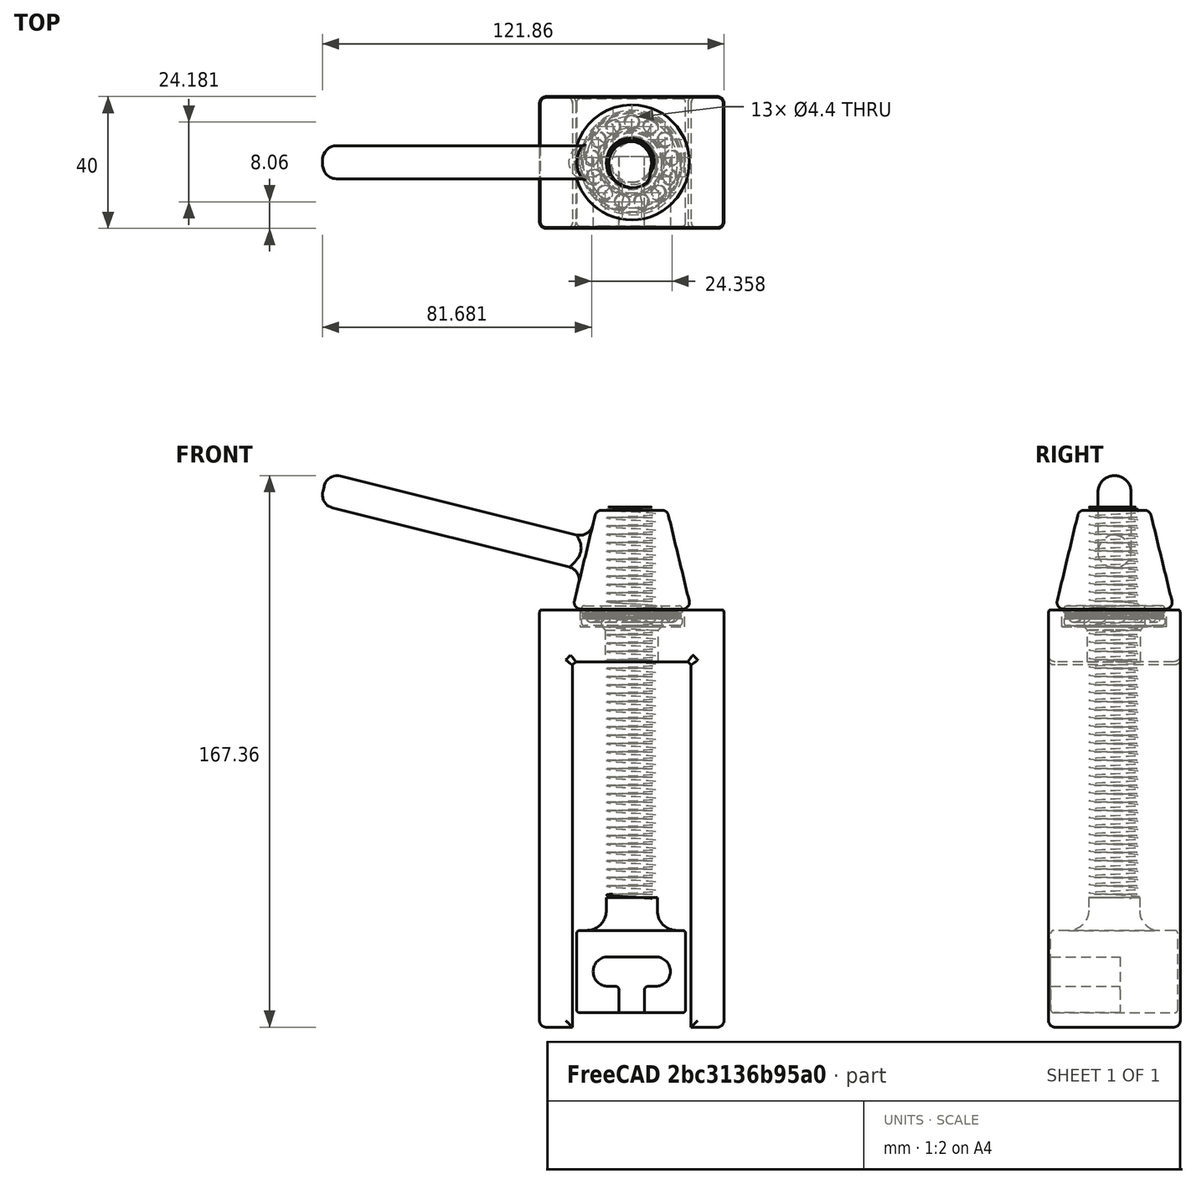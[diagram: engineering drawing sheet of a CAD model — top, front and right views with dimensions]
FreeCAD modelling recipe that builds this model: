
FCSTD DOCUMENT  (FreeCAD 0.21R33771 (Git))
Label: sjemnik
License: All rights reserved
LicenseURL: http://en.wikipedia.org/wiki/All_rights_reserved
objects: Sketcher::SketchObject×25, PartDesign::Fillet×14, PartDesign::Pad×9, PartDesign::Pocket×8, PartDesign::Body×8, PartDesign::Chamfer×3, PartDesign::Plane×3, Part::Part2DObjectPython×2, Part::Helix×2, PartDesign::AdditivePipe×2, PartDesign::Groove×2, PartDesign::CoordinateSystem×1, PartDesign::Line×1, PartDesign::Revolution×1, Part::FeaturePython×1, PartDesign::PolarPattern×1, PartDesign::AdditiveLoft×1, Part::Cut×1
note: 125 computed .brp shape members not serialized (recipe doc carries the construction recipe); baked Part::Feature solids carry a one-line shape summary decoded from their .brp

FEATURE [Sketcher::SketchObject] Sketch
  FullyConstrained = false
  MapMode = 5
  Placement = pos=(0,0,0) rot=(1,0,0;1.5708rad)
  Support = -> [XZ_Plane]
  sketch-geometry (8):
    g0: LineSegment StartX=18 StartY=17.0219 StartZ=0 EndX=-18 EndY=17.0219 EndZ=0
    g1: LineSegment StartX=-18 StartY=17.0219 StartZ=0 EndX=-18 EndY=-93.8501 EndZ=0
    g2: LineSegment StartX=-18 StartY=-93.8501 StartZ=0 EndX=-28 EndY=-93.8501 EndZ=0
    g3: LineSegment StartX=-28 StartY=-93.8501 StartZ=0 EndX=-28 EndY=33.6857 EndZ=0
    g4: LineSegment StartX=28 StartY=33.6857 StartZ=0 EndX=-28 EndY=33.6857 EndZ=0
    g5: LineSegment StartX=18 StartY=17.0219 StartZ=0 EndX=18 EndY=-93.8501 EndZ=0
    g6: LineSegment StartX=18 StartY=-93.8501 StartZ=0 EndX=28 EndY=-93.8501 EndZ=0
    g7: LineSegment StartX=28 StartY=-93.8501 StartZ=0 EndX=28 EndY=33.6857 EndZ=0
  constraints (20):
    c: Horizontal(g0)
    c: Symmetric(g4,g3,g-2)
    c: Coincident(g1,g2)
    c: Coincident(g2,g3)
    c: Horizontal(g2)
    c: Vertical(g1)
    c: Vertical(g3)
    c: Coincident(g5,g6)
    c: Coincident(g6,g7)
    c: Coincident(g7,g4)
    c: Horizontal(g6)
    c: Vertical(g5)
    c: Vertical(g7)
    c: Equal(g2,g6)
    c: Coincident(g5,g0)
    c: Coincident(g0,g1)
    c: Coincident(g4,g3)
    c: Equal(g1,g5)
    c: Distance(g4) = 56
    c: Distance(g0) = 36
FEATURE [PartDesign::Pad] Pad
  Direction = (0,-1,2e-16)
  Length = 40
  Length2 = 10
  Placement = pos=(0,0,0) rot=(1,0,0;1.5708rad)
  Profile = -> Sketch
  ReferenceAxis = -> Sketch [N_Axis]
  Refine = true
  Type = 0
FEATURE [PartDesign::Fillet] Fillet
  Base = -> Pad [Face5,Face10,Face6,Face4,Face9]
  BaseFeature = -> Pad
  Placement = pos=(0,0,0) rot=(1,0,0;1.5708rad)
  Radius = 2
  Refine = true
  SupportTransform = false
  UseAllEdges = false
FEATURE [PartDesign::Chamfer] Chamfer
  Angle = 45
  Base = -> Fillet [Edge1,Edge4]
  BaseFeature = -> Fillet
  ChamferType = 0
  FlipDirection = false
  Placement = pos=(0,0,0) rot=(1,0,0;1.5708rad)
  Refine = true
  Size = 1
  Size2 = 1
  SupportTransform = false
  UseAllEdges = false
FEATURE [Sketcher::SketchObject] Sketch001
  FullyConstrained = false
  MapMode = 5
  Placement = pos=(0,2.23e-14,33.6857) rot=(0,0,1;3.14159rad)
  Support = -> [Chamfer]
  sketch-geometry (2):
    g0: Circle CenterX=-0.164408 CenterY=20.0241 CenterZ=0 NormalX=0 NormalY=0 NormalZ=1 AngleXU=0 Radius=20.0248
    g1: Circle CenterX=-0.164408 CenterY=20.0241 CenterZ=0 NormalX=0 NormalY=0 NormalZ=1 AngleXU=0 Radius=15.8641
  constraints (2):
    c: PointOnObject(g-1,g0)
    c: Coincident(g1,g0)
FEATURE [PartDesign::Pocket] Pocket
  BaseFeature = -> Chamfer
  Direction = (0,0,-1)
  Length = 6
  Length2 = 5
  Placement = pos=(0,0,0) rot=(1,0,0;1.5708rad)
  Profile = -> Sketch001
  ReferenceAxis = -> Sketch001 [N_Axis]
  Refine = true
  Type = 0
FEATURE [PartDesign::Fillet] Fillet001
  Base = -> Pocket [Edge85]
  BaseFeature = -> Pocket
  Placement = pos=(0,0,0) rot=(1,0,0;1.5708rad)
  Radius = 1
  Refine = true
  SupportTransform = false
  UseAllEdges = false
FEATURE [Sketcher::SketchObject] Sketch002
  FullyConstrained = false
  MapMode = 5
  Placement = pos=(0,6.1e-15,27.6857) rot=(0,0,1;3.14159rad)
  Support = -> [Fillet001]
  sketch-geometry (1):
    g0: Circle CenterX=0 CenterY=20.1421 CenterZ=0 NormalX=0 NormalY=0 NormalZ=1 AngleXU=0 Radius=8.03905
  constraints (1):
    c: PointOnObject(g0,g-2)
FEATURE [PartDesign::Pocket] Pocket001
  BaseFeature = -> Fillet001
  Direction = (0,2e-16,-1)
  Length = 15
  Length2 = 5
  Placement = pos=(0,0,0) rot=(1,0,0;1.5708rad)
  Profile = -> Sketch002
  ReferenceAxis = -> Sketch002 [N_Axis]
  Refine = true
  Type = 0
FEATURE [PartDesign::Chamfer] Chamfer001
  Angle = 45
  Base = -> Pocket001 [Edge54]
  BaseFeature = -> Pocket001
  ChamferType = 0
  FlipDirection = false
  Placement = pos=(0,0,0) rot=(1,0,0;1.5708rad)
  Refine = true
  Size = 1
  Size2 = 1
  SupportTransform = false
  UseAllEdges = false
FEATURE [Sketcher::SketchObject] Sketch003
  FullyConstrained = false
  MapMode = 5
  Support = -> [XY_Plane001]
  sketch-geometry (4):
    g0: LineSegment StartX=16.3519 StartY=-0.720672 StartZ=0 EndX=-16.7624 EndY=-0.720672 EndZ=0
    g1: LineSegment StartX=-16.7624 StartY=-0.720672 StartZ=0 EndX=-16.7624 EndY=-39.3105 EndZ=0
    g2: LineSegment StartX=-16.7624 StartY=-39.3105 StartZ=0 EndX=16.3519 EndY=-39.3105 EndZ=0
    g3: LineSegment StartX=16.3519 StartY=-39.3105 StartZ=0 EndX=16.3519 EndY=-0.720672 EndZ=0
  constraints (8):
    c: Coincident(g0,g1)
    c: Coincident(g1,g2)
    c: Coincident(g2,g3)
    c: Coincident(g3,g0)
    c: Horizontal(g0)
    c: Horizontal(g2)
    c: Vertical(g1)
    c: Vertical(g3)
FEATURE [PartDesign::Pad] Pad001
  Direction = (0,0,1)
  Length = 25
  Length2 = 10
  Midplane = true
  Profile = -> Sketch003
  ReferenceAxis = -> Sketch003 [N_Axis]
  Refine = true
  Type = 0
FEATURE [PartDesign::Fillet] Fillet002
  Base = -> Pad001 [Face6,Face3,Face5,Face1,Face2]
  BaseFeature = -> Pad001
  Radius = 1
  Refine = true
  SupportTransform = false
  UseAllEdges = false
FEATURE [Sketcher::SketchObject] Sketch004
  FullyConstrained = false
  MapMode = 5
  Placement = pos=(0,-39.3105,0) rot=(1,0,0;1.5708rad)
  Support = -> [Fillet002]
  sketch-geometry (8):
    g0: ArcOfCircle CenterX=0 CenterY=-15.596 CenterZ=0 NormalX=0 NormalY=0 NormalZ=1 AngleXU=0 Radius=3.88762 StartAngle=3.14159 EndAngle=6.28319
    g1: LineSegment StartX=-3.88762 StartY=-4.48111 StartZ=0 EndX=-3.88762 EndY=-15.596 EndZ=0
    g2: LineSegment StartX=3.88762 StartY=-15.596 StartZ=0 EndX=3.88762 EndY=-4.48111 EndZ=0
    g3: ArcOfCircle CenterX=-7.23544 CenterY=0 CenterZ=0 NormalX=0 NormalY=0 NormalZ=1 AngleXU=0 Radius=4.48111 StartAngle=1.5708 EndAngle=4.71239
    g4: ArcOfCircle CenterX=7.23544 CenterY=0 CenterZ=0 NormalX=0 NormalY=0 NormalZ=1 AngleXU=0 Radius=4.48111 StartAngle=4.71239 EndAngle=7.85398
    g5: LineSegment StartX=-7.23544 StartY=-4.48111 StartZ=0 EndX=-3.88762 EndY=-4.48111 EndZ=0
    g6: LineSegment StartX=7.23544 StartY=4.48111 StartZ=0 EndX=-7.23544 EndY=4.48111 EndZ=0
    g7: LineSegment StartX=3.88762 StartY=-4.48111 StartZ=0 EndX=7.23544 EndY=-4.48111 EndZ=0
  constraints (11):
    c: Tangent(g1,g0) = -1.5708
    c: Tangent(g0,g2) = -1.5708
    c: PointOnObject(g0,g-2)
    c: Tangent(g3,g5) = -1.5708
    c: Coincident(g7,g4) = -1.5708
    c: Tangent(g4,g6) = -1.5708
    c: Tangent(g6,g3) = -1.5708
    c: Equal(g3,g4)
    c: PointOnObject(g3,g-1)
    c: Coincident(g5,g1)
    c: Coincident(g7,g2)
FEATURE [PartDesign::Pocket] Pocket002
  BaseFeature = -> Fillet002
  Direction = (0,1,-2e-16)
  Length = 21
  Length2 = 5
  Profile = -> Sketch004
  ReferenceAxis = -> Sketch004 [N_Axis]
  Refine = true
  Type = 0
FEATURE [PartDesign::Fillet] Fillet003
  Base = -> Pocket002 [Edge68,Edge58]
  BaseFeature = -> Pocket002
  Radius = 1
  Refine = true
  SupportTransform = false
  UseAllEdges = false
FEATURE [Sketcher::SketchObject] Sketch005
  FullyConstrained = false
  MapMode = 5
  Placement = pos=(0,0,12.5) rot=(0,0,1;0rad)
  Support = -> [Fillet003]
  sketch-geometry (1):
    g0: Circle CenterX=0 CenterY=-20.0878 CenterZ=0 NormalX=0 NormalY=0 NormalZ=1 AngleXU=0 Radius=7.73926
  constraints (1):
    c: PointOnObject(g0,g-2)
FEATURE [PartDesign::Pad] Pad002
  BaseFeature = -> Fillet003
  Direction = (0,0,1)
  Length = 10
  Length2 = 10
  Profile = -> Sketch005
  ReferenceAxis = -> Sketch005 [N_Axis]
  Refine = true
  Type = 0
FEATURE [Part::Part2DObjectPython] BThreadProfile  # Draft 2D object (typed FeaturePython)
  Area = 145.406
  Closed = true
  Continuity = C2
  Height = 120
  Helix = Helix
  Instructions = Expand this with the ... button to view instructions | Sweep this object along a helix of the same pitch to produce your thread. | It is recommended to make the helix in the ThreadProfile workbench. | If there is an active Body the ThreadProfile object will be put into it.,If not it can be dragged and dropped into the body later. | If there is an active Body when the helix is made there will be made a ShapeBinder for it | For internal threads you will need to cut the Sweep object out of a cylinder, or if using Part Design sweep it as a Subtractive Pipe. | Always use Frenet mode | I have provided some presets, but it is possible there could be some errors.  Double check for mission critical applications. | Also, the tolerances might be different from what you wish to have.  I believe the internal minor diameters are all minimum and the external are all maximum.
  InternalOrExternal = 1
  MakeFace = true
  MinorDiameter = 12
  Parameterization = 1
  Pitch = 2.54
  Placement = pos=(0,-20,22) rot=(0,0,1;0rad)
  Points = (120) [(7.64394,0.40116,0),(7.44097,0.783173,0),(7.21944,1.14506,0),(6.98089,1.48596,0),(6.72693,1.8051,0),(6.45915,2.10183,0),(6.17921,2.37559,0),+113 more]
  Presets = 0
  Quality = 6
  ThreadCount = 47.2441
  Variants = 0
  Version = 1.89
  external2S_data = [-0.00461051,-0.00886426,-0.0128148,-0.0165028,-0.0199596,-0.0232105,-0.0262759,-0.0291725,-0.0319145,-0.0345137,-0.0369805,-0.0393235,-0.0415505,-0.0436681,-0.0456823,-0.0475981,-0.0494204,-0.0511532,-0.0528003,-0.0543649,-0.0558502,+698 more]
  external3S_data = [-0.00677828,-0.0128149,-0.0182584,-0.0232106,-0.0277444,-0.0319145,-0.0357632,-0.0393236,-0.0426227,-0.0456823,-0.0485208,-0.0511533,-0.0535928,-0.0558503,-0.0579353,-0.059856,-0.0616195,-0.0632319,-0.0646984,-0.0660239,-0.0672123,+698 more]
  external45_data = [-0.00137363,-0.00271738,-0.00403219,-0.00531893,-0.00657844,-0.00781148,-0.00901878,-0.010201,-0.0113589,-0.012493,-0.0136039,-0.0146921,-0.0157583,-0.0168028,-0.0178261,-0.0188288,-0.0198112,-0.0207738,-0.0217169,-0.0226409,-0.0235462,+698 more]
  external_data = [0.651362,0.640051,0.628739,0.617428,0.606116,0.594804,0.583493,0.572181,0.56087,0.549558,0.538246,0.526935,0.515623,0.504312,0.493,0.481688,0.470377,0.459065,0.447754,0.436442,0.42513,0.413819,0.402507,0.391196,0.379884,0.368572,0.357261,+692 more]
  internal2S_data = [0,0,0,0,0,0,0,0,0,0,0,0,0,0,0,0,0,0,0,0,0,0,0,0,0,0,0,0,0,0,0,0,0,0,0,0,0,0,0,0,0,0,0,0,0,0,0,0,0,0,0,0,0,0,0,0,0,0,0,0,0,0,0,0,0,0,0,0,0,0,0,0,0,0,0,0,0,0,0,0,0,0,0,0,0,0,0,0,0,0,0.00481128,0.00962256,0.0144338,0.0192451,0.0240564,+624 more]
  internal3S_data = [0,0,0,0,0,0,0,0,0,0,0,0,0,0,0,0,0,0,0,0,0,0,0,0,0,0,0,0,0,0,0,0,0,0,0,0,0,0,0,0,0,0,0,0,0,0,0,0,0,0,0,0,0,0,0,0,0,0,0,0,0.00721688,0.0144338,0.0216506,0.0288675,0.0360844,0.0433013,0.0505181,0.057735,0.0649519,0.0721688,0.0793857,0.0866025,+647 more]
  internal45_data = [0,0,0,0,0,0,0,0,0,0,0,0,0,0,0,0,0,0,0,0,0,0,0,0,0,0,0,0,0,0,0,0,0,0,0,0,0,0,0,0,0,0,0,0,0,0,0,0,0,0,0,0,0,0,0,0,0,0,0,0,0,0,0,0,0,0,0,0,0,0,0,0,0,0,0,0,0,0,0,0,0,0,0,0,0,0,0,0,0,0,0,0,0,0,0,0,0,0,0,0,0,0,0,0,0,0,0,0,0,0,0,0,0,0,0,0,0,0,0,0,+599 more]
  internal_data = [0.6514,0.640089,0.628777,0.617466,0.606154,0.594842,0.583531,0.572219,0.560908,0.549596,0.538284,0.526973,0.515661,0.50435,0.493038,0.481727,0.470415,0.459103,0.447792,0.43648,0.425169,0.413857,0.402545,0.391234,0.379922,0.368611,0.357299,+692 more]
  preset_names = Buttress presets | 1/2-12 | 1/2-16 | 1/2-20 | 5/8-12 | 5/8-16 | 5/8-20 | 3/4-12 | 3/4-16 | 3/4-20 | 7/8-10 | 7/8-12 | 7/8-16 | 1-10 | 1-12 | 1-16 | 1 1/4-8 | 1 1/4-10 | 1 1/4-12 | 1 3/8-8 | 1 3/8-10 | 1 3/8-12 | 1 1/2-8 | 1 1/2-10 | 1 1/2-12 | 1 3/4-6 | 1 3/4-6 | 1 3/4-10 | 2-6 | 2-8 | 2-10 | 2 1/4-6 | 2 1/4-8 | 2 1/4-10 | 2 1/2-6 | 2 1/2-8 | 2 1/2-10 | 2 3/4-5 | 2 3/4-6 | 2 3/4-8 | 3-5 | 3-6 | 3-8 | 3 1/2-5 | 3 1/2-6 | 3 1/2-8 | 4-5 | 4-6 | 4-8 | 4 1/2-4 | 4 1/2-5 | 4 1/2-6 | 5-4 | 5-5 | 5-6 | 5 1/2-4 | 5 1/2-5 | 5 1/2-6 | 6-4 | 6-5 | 6-6 | 7-3 | 7-4 | 7-5 | 8-3 | 8-4 | 8-5 | 9-3 | 9-4 | 9-5 | 10-3 | 10-4 | 10-5 | 11-2.5 | 11-3 | 11-4 | 12-2.5 | 12-3 | 12-4 | 13-2.5 | 13-3 | 13-4 | 14-2.5 | 14-3 | 14-4 | 16-2.5 | 16-3 | 16-4 | 18-2 | 18-2.5 | 18-3 | 20-2 | 20-2.5 | 20-3 | 22-2 | 22-2.5 | 22-3 | 24-2 | 24-2.5 | 24-3
  presets_data = [0,0,0,2.11667,11.2674,11.3271,1.5875,11.6214,11.6745,1.27,11.8342,11.8826,2.11667,14.442,14.5025,1.5875,14.7961,14.8498,1.27,15.0088,15.0579,2.11667,17.6167,17.6778,1.5875,17.9708,18.0251,1.27,18.1835,18.2332,2.54,20.5085,20.575,2.11667,+266 more]
FEATURE [Part::Helix] Helix
  Angle = 0
  AttacherType = Attacher::AttachEngine3D
  Height = 120
  LocalCoord = 0
  Pitch = 2.54
  Placement = pos=(0,-20,21) rot=(0,0,1;0rad)
  Radius = 1
  SegmentLength = 1
  Style = 0
  expr: AttachmentOffset = BThreadProfile.AttachmentOffset
  expr: Height = BThreadProfile001.ThreadCount * BThreadProfile001.Pitch
  expr: MapMode = BThreadProfile.MapMode
  expr: MapPathParameter = BThreadProfile.MapPathParameter
  expr: MapReversed = BThreadProfile.MapReversed
  expr: Pitch = BThreadProfile001.Pitch
  expr: SegmentLength = 1
  expr: Support = BThreadProfile.Support
FEATURE [PartDesign::Fillet] Fillet004
  Base = -> Pad002 [Edge71]
  BaseFeature = -> Pad002
  Radius = 6
  Refine = true
  SupportTransform = false
  UseAllEdges = false
FEATURE [PartDesign::AdditivePipe] AdditivePipe
  AuxilleryCurvelinear = true
  AuxillerySpineTangent = false
  BaseFeature = -> Fillet004
  Binormal = (0,0,0)
  Mode = 2
  Profile = -> BThreadProfile
  Refine = true
  Spine = -> Helix
  SpineTangent = false
  Transformation = 0
  Transition = 0
FEATURE [PartDesign::Body] Body001  label="sjemnik"
  Group = -> [Sketch003,Pad001,Fillet002,Sketch004,Pocket002,Fillet003,Sketch005,Pad002,BThreadProfile,Helix,Fillet004,AdditivePipe]
  Origin = -> Origin001
  Placement = pos=(0,0,-77) rot=(0,0,1;0rad)
  Tip = -> AdditivePipe
FEATURE [Sketcher::SketchObject] Sketch006
  FullyConstrained = false
  MapMode = 5
  Support = -> [XY_Plane002]
  sketch-geometry (2):
    g0: Circle CenterX=0 CenterY=-19.9835 CenterZ=0 NormalX=0 NormalY=0 NormalZ=1 AngleXU=0 Radius=15.3466
    g1: Circle CenterX=0 CenterY=-19.9835 CenterZ=0 NormalX=0 NormalY=0 NormalZ=1 AngleXU=0 Radius=9.19294
  constraints (2):
    c: PointOnObject(g0,g-2)
    c: Coincident(g1,g0)
FEATURE [PartDesign::Pad] Pad003
  Direction = (0,0,1)
  Length = 3
  Length2 = 10
  Profile = -> Sketch006
  ReferenceAxis = -> Sketch006 [N_Axis]
  Refine = true
  Type = 0
FEATURE [PartDesign::Fillet] Fillet005
  Base = -> Pad003 [Face4]
  BaseFeature = -> Pad003
  Radius = 0.5
  Refine = true
  SupportTransform = false
  UseAllEdges = false
FEATURE [Sketcher::SketchObject] Sketch007
  FullyConstrained = false
  MapMode = 5
  Placement = pos=(0,0,3) rot=(0,0,1;0rad)
  Support = -> [Fillet005]
  sketch-geometry (1):
    g0: Circle CenterX=0 CenterY=-19.9159 CenterZ=0 NormalX=0 NormalY=0 NormalZ=1 AngleXU=0 Radius=12.4278
  constraints (1):
    c: PointOnObject(g0,g-2)
FEATURE [PartDesign::Plane] DatumPlane
  Length = 71.2997
  MapMode = 4
  Placement = pos=(0,0,3) rot=(0.57735,0.57735,0.57735;2.0944rad)
  ResizeMode = 0
  Support = -> [Sketch007]
  Width = 60.9833
FEATURE [Sketcher::SketchObject] Sketch008
  FullyConstrained = false
  MapMode = 5
  Placement = pos=(0,0,3) rot=(0.57735,0.57735,0.57735;2.0944rad)
  Support = -> [DatumPlane]
  sketch-geometry (1):
    g0: Circle CenterX=-7.76411 CenterY=0 CenterZ=0 NormalX=0 NormalY=0 NormalZ=1 AngleXU=0 Radius=2
  constraints (2):
    c: PointOnObject(g0,g-1)
    c: Radius(g0) = 2
FEATURE [PartDesign::Groove] Groove
  Angle = 360
  Axis = (0,0,1)
  Base = (0,-19.9159,3)
  BaseFeature = -> Fillet005
  Profile = -> Sketch008
  ReferenceAxis = -> Sketch007 [Edge1]
  Refine = true
FEATURE [Sketcher::SketchObject] Sketch009
  FullyConstrained = false
  MapMode = 5
  Placement = pos=(0,0,3) rot=(0,0,1;0rad)
  Support = -> [Fillet005]
  sketch-geometry (1):
    g0: Circle CenterX=0 CenterY=-19.9159 CenterZ=0 NormalX=0 NormalY=0 NormalZ=1 AngleXU=0 Radius=12.4278
  constraints (1):
    c: PointOnObject(g0,g-2)
FEATURE [Sketcher::SketchObject] Sketch010
  FullyConstrained = false
  MapMode = 5
  Placement = pos=(0,0,3) rot=(0.57735,0.57735,0.57735;2.0944rad)
  Support = -> [DatumPlane]
  sketch-geometry (2):
    g0: ArcOfCircle CenterX=-7.76411 CenterY=0 CenterZ=0 NormalX=0 NormalY=0 NormalZ=1 AngleXU=0 Radius=2 StartAngle=0.0015635 EndAngle=3.14003
    g1: LineSegment StartX=-9.76411 StartY=0.003127 StartZ=0 EndX=-5.76411 EndY=0.003127 EndZ=0
  constraints (5):
    c: PointOnObject(g0,g-1)
    c: Radius(g0) = 2
    c: Horizontal(g1)
    c: Coincident(g0,g1)
    c: Coincident(g0,g1)
FEATURE [PartDesign::CoordinateSystem] Local_CS
  AttacherType = Attacher::AttachEngine3D
  MapMode = 11
  Placement = pos=(-1.8e-15,-19.9159,3) rot=(0,0,1;1.5708rad)
  Support = -> [Sketch009]
FEATURE [PartDesign::Line] DatumLine
  AttacherType = Attacher::AttachEngineLine
  Length = 20
  MapMode = 18
  Placement = pos=(-1.8e-15,-19.9159,3) rot=(0,0,1;1.5708rad)
  ResizeMode = 0
  Support = -> [Local_CS]
FEATURE [PartDesign::Revolution] Revolution
  Angle = 360
  Axis = (0,1,0)
  Base = (0,0,3)
  Placement = pos=(0,0,3) rot=(0.57735,0.57735,0.57735;2.0944rad)
  Profile = -> Sketch010
  ReferenceAxis = -> Sketch010 [H_Axis]
  Refine = true
FEATURE [PartDesign::Body] Body003  label="sharik"
  Group = -> [Sketch009,Sketch010,Revolution]
  Origin = -> Origin003
  Tip = -> Revolution
FEATURE [Part::FeaturePython] Array  # Draft array (typed FeaturePython)
  Angle = 360
  ArrayType = 1
  Axis = (0,0,1)
  Base = -> Body003
  Center = (0,-19.92,0)
  Count = 13
  Fuse = false
  IntervalAxis = (0,0,0)
  IntervalX = (50,0,0)
  IntervalY = (0,50,0)
  IntervalZ = (0,0,50)
  NumberCircles = 3
  NumberPolar = 13
  NumberX = 2
  NumberY = 2
  NumberZ = 1
  Placement = pos=(0,0,28) rot=(0,0,1;0rad)
  RadialDistance = 50
  Symmetry = 1
  TangentialDistance = 25
FEATURE [Sketcher::SketchObject] Sketch011
  FullyConstrained = false
  MapMode = 5
  Support = -> [XY_Plane004]
  sketch-geometry (2):
    g0: Circle CenterX=0 CenterY=-19.9835 CenterZ=0 NormalX=0 NormalY=0 NormalZ=1 AngleXU=0 Radius=15.3466
    g1: Circle CenterX=0 CenterY=-19.9835 CenterZ=0 NormalX=0 NormalY=0 NormalZ=1 AngleXU=0 Radius=9.19294
  constraints (2):
    c: PointOnObject(g0,g-2)
    c: Coincident(g1,g0)
FEATURE [PartDesign::Pad] Pad004
  Direction = (0,0,1)
  Length = 3
  Length2 = 10
  Profile = -> Sketch011
  ReferenceAxis = -> Sketch011 [N_Axis]
  Refine = true
  Type = 0
FEATURE [PartDesign::Fillet] Fillet006
  Base = -> Pad004 [Face4]
  BaseFeature = -> Pad004
  Radius = 0.5
  Refine = true
  SupportTransform = false
  UseAllEdges = false
FEATURE [Sketcher::SketchObject] Sketch012
  FullyConstrained = false
  MapMode = 5
  Placement = pos=(0,0,3) rot=(0,0,1;0rad)
  Support = -> [Fillet006]
  sketch-geometry (1):
    g0: Circle CenterX=0 CenterY=-19.9159 CenterZ=0 NormalX=0 NormalY=0 NormalZ=1 AngleXU=0 Radius=12.4278
  constraints (1):
    c: PointOnObject(g0,g-2)
FEATURE [PartDesign::Plane] DatumPlane001
  Length = 71.2997
  MapMode = 4
  Placement = pos=(0,0,3) rot=(0.57735,0.57735,0.57735;2.0944rad)
  ResizeMode = 0
  Support = -> [Sketch012]
  Width = 60.9833
FEATURE [Sketcher::SketchObject] Sketch013
  FullyConstrained = false
  MapMode = 5
  Placement = pos=(0,0,3) rot=(0.57735,0.57735,0.57735;2.0944rad)
  Support = -> [DatumPlane001]
  sketch-geometry (1):
    g0: Circle CenterX=-7.76411 CenterY=0 CenterZ=0 NormalX=0 NormalY=0 NormalZ=1 AngleXU=0 Radius=2
  constraints (2):
    c: PointOnObject(g0,g-1)
    c: Radius(g0) = 2
FEATURE [PartDesign::Groove] Groove001
  Angle = 360
  Axis = (0,0,1)
  Base = (0,-19.9159,3)
  BaseFeature = -> Fillet006
  Profile = -> Sketch013
  ReferenceAxis = -> Sketch012 [Edge1]
  Refine = true
FEATURE [PartDesign::Fillet] Fillet007
  Base = -> Groove001 [Edge3]
  BaseFeature = -> Groove001
  Radius = 1
  Refine = true
  SupportTransform = false
  UseAllEdges = false
FEATURE [Sketcher::SketchObject] Sketch014
  FullyConstrained = false
  MapMode = 5
  Support = -> [XY_Plane005]
  sketch-geometry (2):
    g0: Circle CenterX=0 CenterY=-20.0278 CenterZ=0 NormalX=0 NormalY=0 NormalZ=1 AngleXU=0 Radius=15.0197
    g1: Circle CenterX=0 CenterY=-20.0278 CenterZ=0 NormalX=0 NormalY=0 NormalZ=1 AngleXU=0 Radius=9.6161
  constraints (2):
    c: PointOnObject(g0,g-2)
    c: Coincident(g1,g0)
FEATURE [PartDesign::Pad] Pad005
  Direction = (0,0,1)
  Length = 1
  Length2 = 10
  Profile = -> Sketch014
  ReferenceAxis = -> Sketch014 [N_Axis]
  Refine = true
  Type = 0
FEATURE [Sketcher::SketchObject] Sketch015
  FullyConstrained = false
  MapMode = 5
  Placement = pos=(0,0,1) rot=(0,0,1;0rad)
  Support = -> [Pad005]
  sketch-geometry (1):
    g0: Circle CenterX=0 CenterY=-7.75919 CenterZ=0 NormalX=0 NormalY=0 NormalZ=1 AngleXU=0 Radius=2.2
  constraints (2):
    c: PointOnObject(g0,g-2)
    c: Radius(g0) = 2.2
FEATURE [PartDesign::Pocket] Pocket003
  BaseFeature = -> Pad005
  Direction = (0,0,-1)
  Length = 5
  Length2 = 5
  Profile = -> Sketch015
  ReferenceAxis = -> Sketch015 [N_Axis]
  Refine = true
  Type = 0
FEATURE [PartDesign::PolarPattern] PolarPattern
  Angle = 360
  Axis = -> Pocket003 [Edge3]
  BaseFeature = -> Pocket003
  Occurrences = 13
  Originals = -> [Pocket003]
  Refine = true
FEATURE [PartDesign::Chamfer] Chamfer002
  Angle = 45
  Base = -> PolarPattern [Face3,Face2]
  BaseFeature = -> PolarPattern
  ChamferType = 0
  FlipDirection = false
  Refine = true
  Size = 0.2
  Size2 = 1
  SupportTransform = false
  UseAllEdges = false
FEATURE [PartDesign::Body] Body005  label="separator"
  Group = -> [Sketch014,Pad005,Sketch015,Pocket003,PolarPattern,Chamfer002]
  Origin = -> Origin005
  Placement = pos=(0,0,30.5) rot=(0,0,1;0rad)
  Tip = -> Chamfer002
FEATURE [Sketcher::SketchObject] Sketch016
  FullyConstrained = false
  MapMode = 5
  Placement = pos=(0,0,3) rot=(0,0,1;0rad)
  Support = -> [Fillet007]
  sketch-geometry (4):
    g0: LineSegment StartX=-18.0338 StartY=-2.72149 StartZ=0 EndX=19.1148 EndY=-2.72149 EndZ=0
    g1: LineSegment StartX=19.1148 StartY=-2.72149 StartZ=0 EndX=19.1148 EndY=-36.5495 EndZ=0
    g2: LineSegment StartX=19.1148 StartY=-36.5495 StartZ=0 EndX=-18.0338 EndY=-36.5495 EndZ=0
    g3: LineSegment StartX=-18.0338 StartY=-36.5495 StartZ=0 EndX=-18.0338 EndY=-2.72149 EndZ=0
  constraints (8):
    c: Coincident(g0,g1)
    c: Coincident(g1,g2)
    c: Coincident(g2,g3)
    c: Coincident(g3,g0)
    c: Horizontal(g0)
    c: Horizontal(g2)
    c: Vertical(g1)
    c: Vertical(g3)
FEATURE [PartDesign::Pocket] Pocket004
  BaseFeature = -> Fillet007
  Direction = (0,0,-1)
  Length = 1
  Length2 = 5
  Profile = -> Sketch016
  ReferenceAxis = -> Sketch016 [N_Axis]
  Refine = true
  Type = 0
FEATURE [PartDesign::Body] Body004  label="obojma2"
  Group = -> [Sketch011,Pad004,Fillet006,Sketch012,DatumPlane001,Sketch013,Groove001,Fillet007,Sketch016,Pocket004]
  Origin = -> Origin004
  Placement = pos=(0,0,34) rot=(0,1,0;3.14159rad)
  Tip = -> Pocket004
FEATURE [Sketcher::SketchObject] Sketch017
  FullyConstrained = false
  MapMode = 5
  Placement = pos=(0,0,3) rot=(0,0,1;0rad)
  Support = -> [Groove]
  sketch-geometry (4):
    g0: LineSegment StartX=-21.0107 StartY=-2.45448 StartZ=0 EndX=21.2563 EndY=-2.45448 EndZ=0
    g1: LineSegment StartX=21.2563 StartY=-2.45448 StartZ=0 EndX=21.2563 EndY=-37.7881 EndZ=0
    g2: LineSegment StartX=21.2563 StartY=-37.7881 StartZ=0 EndX=-21.0107 EndY=-37.7881 EndZ=0
    g3: LineSegment StartX=-21.0107 StartY=-37.7881 StartZ=0 EndX=-21.0107 EndY=-2.45448 EndZ=0
  constraints (8):
    c: Coincident(g0,g1)
    c: Coincident(g1,g2)
    c: Coincident(g2,g3)
    c: Coincident(g3,g0)
    c: Horizontal(g0)
    c: Horizontal(g2)
    c: Vertical(g1)
    c: Vertical(g3)
FEATURE [PartDesign::Pocket] Pocket005
  BaseFeature = -> Groove
  Direction = (0,0,-1)
  Length = 1
  Length2 = 5
  Profile = -> Sketch017
  ReferenceAxis = -> Sketch017 [N_Axis]
  Refine = true
  Type = 0
FEATURE [PartDesign::Fillet] Fillet008
  Base = -> Pocket005 [Edge1]
  BaseFeature = -> Pocket005
  Radius = 1
  Refine = true
  SupportTransform = false
  UseAllEdges = false
FEATURE [PartDesign::Body] Body002  label="obojma1"
  Group = -> [Sketch006,Pad003,Fillet005,Sketch007,DatumPlane,Sketch008,Groove,Sketch017,Pocket005,Fillet008]
  Origin = -> Origin002
  Placement = pos=(0,0,28) rot=(0,0,1;0rad)
  Tip = -> Fillet008
FEATURE [Sketcher::SketchObject] Sketch018
  FullyConstrained = false
  MapMode = 5
  Placement = pos=(0,2.23e-14,33.6857) rot=(0,0,1;3.14159rad)
  Support = -> [Chamfer001]
  sketch-geometry (4):
    g0: LineSegment StartX=-30.527 StartY=41.5704 StartZ=0 EndX=32.0367 EndY=41.5704 EndZ=0
    g1: LineSegment StartX=32.0367 StartY=41.5704 StartZ=0 EndX=32.0367 EndY=-0.704765 EndZ=0
    g2: LineSegment StartX=32.0367 StartY=-0.704765 StartZ=0 EndX=-30.527 EndY=-0.704765 EndZ=0
    g3: LineSegment StartX=-30.527 StartY=-0.704765 StartZ=0 EndX=-30.527 EndY=41.5704 EndZ=0
  constraints (8):
    c: Coincident(g0,g1)
    c: Coincident(g1,g2)
    c: Coincident(g2,g3)
    c: Coincident(g3,g0)
    c: Horizontal(g0)
    c: Horizontal(g2)
    c: Vertical(g1)
    c: Vertical(g3)
FEATURE [PartDesign::Pocket] Pocket006
  BaseFeature = -> Chamfer001
  Direction = (0,4e-16,-1)
  Length = 1
  Length2 = 5
  Placement = pos=(0,0,0) rot=(1,0,0;1.5708rad)
  Profile = -> Sketch018
  ReferenceAxis = -> Sketch018 [N_Axis]
  Refine = true
  Type = 0
FEATURE [PartDesign::Body] Body  label="Rama"
  Group = -> [Sketch,Pad,Fillet,Chamfer,Sketch001,Pocket,Fillet001,Sketch002,Pocket001,Chamfer001,Sketch018,Pocket006]
  Origin = -> Origin
  Tip = -> Pocket006
FEATURE [Sketcher::SketchObject] Sketch019
  FullyConstrained = false
  MapMode = 5
  Support = -> [XY_Plane006]
  sketch-geometry (1):
    g0: Circle CenterX=0 CenterY=-19.9398 CenterZ=0 NormalX=0 NormalY=0 NormalZ=1 AngleXU=0 Radius=18
  constraints (2):
    c: PointOnObject(g0,g-2)
    c: Radius(g0) = 18
FEATURE [Sketcher::SketchObject] Sketch020
  AttachmentOffset = pos=(0,0,30) rot=(0,0,1;0rad)
  FullyConstrained = false
  MapMode = 5
  Placement = pos=(0,0,30) rot=(0,0,1;0rad)
  Support = -> [XY_Plane006]
  sketch-geometry (1):
    g0: Circle CenterX=0 CenterY=-20.0008 CenterZ=0 NormalX=0 NormalY=0 NormalZ=1 AngleXU=0 Radius=10.7496
  constraints (1):
    c: PointOnObject(g0,g-2)
FEATURE [PartDesign::AdditiveLoft] AdditiveLoft
  Closed = false
  Profile = -> Sketch019
  Refine = true
  Ruled = false
  Sections = -> [Sketch020]
FEATURE [PartDesign::Fillet] Fillet009
  Base = -> AdditiveLoft [Edge1,Edge3]
  BaseFeature = -> AdditiveLoft
  Radius = 2
  Refine = true
  SupportTransform = false
  UseAllEdges = false
FEATURE [Part::Part2DObjectPython] BThreadProfile001  # Draft 2D object (typed FeaturePython)
  Area = 145.406
  Closed = true
  Continuity = C2
  Height = 120
  Helix = Helix
  Instructions = Expand this with the ... button to view instructions | Sweep this object along a helix of the same pitch to produce your thread. | It is recommended to make the helix in the ThreadProfile workbench. | If there is an active Body the ThreadProfile object will be put into it.,If not it can be dragged and dropped into the body later. | If there is an active Body when the helix is made there will be made a ShapeBinder for it | For internal threads you will need to cut the Sweep object out of a cylinder, or if using Part Design sweep it as a Subtractive Pipe. | Always use Frenet mode | I have provided some presets, but it is possible there could be some errors.  Double check for mission critical applications. | Also, the tolerances might be different from what you wish to have.  I believe the internal minor diameters are all minimum and the external are all maximum.
  InternalOrExternal = 1
  MakeFace = true
  MinorDiameter = 12
  Parameterization = 1
  Pitch = 2.54
  Placement = pos=(0,-20,22) rot=(0,0,1;0rad)
  Points = (120) [(7.64394,0.40116,0),(7.44097,0.783173,0),(7.21944,1.14506,0),(6.98089,1.48596,0),(6.72693,1.8051,0),(6.45915,2.10183,0),(6.17921,2.37559,0),+113 more]
  Presets = 0
  Quality = 6
  ThreadCount = 47.2441
  Variants = 0
  Version = 1.89
  external2S_data = [-0.00461051,-0.00886426,-0.0128148,-0.0165028,-0.0199596,-0.0232105,-0.0262759,-0.0291725,-0.0319145,-0.0345137,-0.0369805,-0.0393235,-0.0415505,-0.0436681,-0.0456823,-0.0475981,-0.0494204,-0.0511532,-0.0528003,-0.0543649,-0.0558502,+698 more]
  external3S_data = [-0.00677828,-0.0128149,-0.0182584,-0.0232106,-0.0277444,-0.0319145,-0.0357632,-0.0393236,-0.0426227,-0.0456823,-0.0485208,-0.0511533,-0.0535928,-0.0558503,-0.0579353,-0.059856,-0.0616195,-0.0632319,-0.0646984,-0.0660239,-0.0672123,+698 more]
  external45_data = [-0.00137363,-0.00271738,-0.00403219,-0.00531893,-0.00657844,-0.00781148,-0.00901878,-0.010201,-0.0113589,-0.012493,-0.0136039,-0.0146921,-0.0157583,-0.0168028,-0.0178261,-0.0188288,-0.0198112,-0.0207738,-0.0217169,-0.0226409,-0.0235462,+698 more]
  external_data = [0.651362,0.640051,0.628739,0.617428,0.606116,0.594804,0.583493,0.572181,0.56087,0.549558,0.538246,0.526935,0.515623,0.504312,0.493,0.481688,0.470377,0.459065,0.447754,0.436442,0.42513,0.413819,0.402507,0.391196,0.379884,0.368572,0.357261,+692 more]
  internal2S_data = [0,0,0,0,0,0,0,0,0,0,0,0,0,0,0,0,0,0,0,0,0,0,0,0,0,0,0,0,0,0,0,0,0,0,0,0,0,0,0,0,0,0,0,0,0,0,0,0,0,0,0,0,0,0,0,0,0,0,0,0,0,0,0,0,0,0,0,0,0,0,0,0,0,0,0,0,0,0,0,0,0,0,0,0,0,0,0,0,0,0,0.00481128,0.00962256,0.0144338,0.0192451,0.0240564,+624 more]
  internal3S_data = [0,0,0,0,0,0,0,0,0,0,0,0,0,0,0,0,0,0,0,0,0,0,0,0,0,0,0,0,0,0,0,0,0,0,0,0,0,0,0,0,0,0,0,0,0,0,0,0,0,0,0,0,0,0,0,0,0,0,0,0,0.00721688,0.0144338,0.0216506,0.0288675,0.0360844,0.0433013,0.0505181,0.057735,0.0649519,0.0721688,0.0793857,0.0866025,+647 more]
  internal45_data = [0,0,0,0,0,0,0,0,0,0,0,0,0,0,0,0,0,0,0,0,0,0,0,0,0,0,0,0,0,0,0,0,0,0,0,0,0,0,0,0,0,0,0,0,0,0,0,0,0,0,0,0,0,0,0,0,0,0,0,0,0,0,0,0,0,0,0,0,0,0,0,0,0,0,0,0,0,0,0,0,0,0,0,0,0,0,0,0,0,0,0,0,0,0,0,0,0,0,0,0,0,0,0,0,0,0,0,0,0,0,0,0,0,0,0,0,0,0,0,0,+599 more]
  internal_data = [0.6514,0.640089,0.628777,0.617466,0.606154,0.594842,0.583531,0.572219,0.560908,0.549596,0.538284,0.526973,0.515661,0.50435,0.493038,0.481727,0.470415,0.459103,0.447792,0.43648,0.425169,0.413857,0.402545,0.391234,0.379922,0.368611,0.357299,+692 more]
  preset_names = Buttress presets | 1/2-12 | 1/2-16 | 1/2-20 | 5/8-12 | 5/8-16 | 5/8-20 | 3/4-12 | 3/4-16 | 3/4-20 | 7/8-10 | 7/8-12 | 7/8-16 | 1-10 | 1-12 | 1-16 | 1 1/4-8 | 1 1/4-10 | 1 1/4-12 | 1 3/8-8 | 1 3/8-10 | 1 3/8-12 | 1 1/2-8 | 1 1/2-10 | 1 1/2-12 | 1 3/4-6 | 1 3/4-6 | 1 3/4-10 | 2-6 | 2-8 | 2-10 | 2 1/4-6 | 2 1/4-8 | 2 1/4-10 | 2 1/2-6 | 2 1/2-8 | 2 1/2-10 | 2 3/4-5 | 2 3/4-6 | 2 3/4-8 | 3-5 | 3-6 | 3-8 | 3 1/2-5 | 3 1/2-6 | 3 1/2-8 | 4-5 | 4-6 | 4-8 | 4 1/2-4 | 4 1/2-5 | 4 1/2-6 | 5-4 | 5-5 | 5-6 | 5 1/2-4 | 5 1/2-5 | 5 1/2-6 | 6-4 | 6-5 | 6-6 | 7-3 | 7-4 | 7-5 | 8-3 | 8-4 | 8-5 | 9-3 | 9-4 | 9-5 | 10-3 | 10-4 | 10-5 | 11-2.5 | 11-3 | 11-4 | 12-2.5 | 12-3 | 12-4 | 13-2.5 | 13-3 | 13-4 | 14-2.5 | 14-3 | 14-4 | 16-2.5 | 16-3 | 16-4 | 18-2 | 18-2.5 | 18-3 | 20-2 | 20-2.5 | 20-3 | 22-2 | 22-2.5 | 22-3 | 24-2 | 24-2.5 | 24-3
  presets_data = [0,0,0,2.11667,11.2674,11.3271,1.5875,11.6214,11.6745,1.27,11.8342,11.8826,2.11667,14.442,14.5025,1.5875,14.7961,14.8498,1.27,15.0088,15.0579,2.11667,17.6167,17.6778,1.5875,17.9708,18.0251,1.27,18.1835,18.2332,2.54,20.5085,20.575,2.11667,+266 more]
FEATURE [Part::Helix] Helix001
  Angle = 0
  AttacherType = Attacher::AttachEngine3D
  Height = 120
  LocalCoord = 0
  Pitch = 2.54
  Placement = pos=(0,-20,21) rot=(0,0,1;0rad)
  Radius = 1
  SegmentLength = 1
  Style = 0
  expr: AttachmentOffset = BThreadProfile001.AttachmentOffset
  expr: Height = BThreadProfile001.ThreadCount * BThreadProfile001.Pitch
  expr: MapMode = BThreadProfile001.MapMode
  expr: MapPathParameter = BThreadProfile001.MapPathParameter
  expr: MapReversed = BThreadProfile001.MapReversed
  expr: Pitch = BThreadProfile001.Pitch
  expr: SegmentLength = 1
  expr: Support = BThreadProfile001.Support
FEATURE [Sketcher::SketchObject] Sketch021
  FullyConstrained = false
  MapMode = 5
  Support = -> [XY_Plane007]
  sketch-geometry (4):
    g0: LineSegment StartX=16.3519 StartY=-0.720672 StartZ=0 EndX=-16.7624 EndY=-0.720672 EndZ=0
    g1: LineSegment StartX=-16.7624 StartY=-0.720672 StartZ=0 EndX=-16.7624 EndY=-39.3105 EndZ=0
    g2: LineSegment StartX=-16.7624 StartY=-39.3105 StartZ=0 EndX=16.3519 EndY=-39.3105 EndZ=0
    g3: LineSegment StartX=16.3519 StartY=-39.3105 StartZ=0 EndX=16.3519 EndY=-0.720672 EndZ=0
  constraints (8):
    c: Coincident(g0,g1)
    c: Coincident(g1,g2)
    c: Coincident(g2,g3)
    c: Coincident(g3,g0)
    c: Horizontal(g0)
    c: Horizontal(g2)
    c: Vertical(g1)
    c: Vertical(g3)
FEATURE [PartDesign::Pad] Pad006
  Direction = (0,0,1)
  Length = 25
  Length2 = 10
  Midplane = true
  Profile = -> Sketch021
  ReferenceAxis = -> Sketch021 [N_Axis]
  Refine = true
  Type = 0
FEATURE [PartDesign::Fillet] Fillet010
  Base = -> Pad006 [Face6,Face3,Face5,Face1,Face2]
  BaseFeature = -> Pad006
  Radius = 1
  Refine = true
  SupportTransform = false
  UseAllEdges = false
FEATURE [Sketcher::SketchObject] Sketch022
  FullyConstrained = false
  MapMode = 5
  Placement = pos=(0,-39.3105,0) rot=(1,0,0;1.5708rad)
  Support = -> [Fillet010]
  sketch-geometry (8):
    g0: ArcOfCircle CenterX=0 CenterY=-15.596 CenterZ=0 NormalX=0 NormalY=0 NormalZ=1 AngleXU=0 Radius=3.88762 StartAngle=3.14159 EndAngle=6.28319
    g1: LineSegment StartX=-3.88762 StartY=-4.48111 StartZ=0 EndX=-3.88762 EndY=-15.596 EndZ=0
    g2: LineSegment StartX=3.88762 StartY=-15.596 StartZ=0 EndX=3.88762 EndY=-4.48111 EndZ=0
    g3: ArcOfCircle CenterX=-7.23544 CenterY=0 CenterZ=0 NormalX=0 NormalY=0 NormalZ=1 AngleXU=0 Radius=4.48111 StartAngle=1.5708 EndAngle=4.71239
    g4: ArcOfCircle CenterX=7.23544 CenterY=0 CenterZ=0 NormalX=0 NormalY=0 NormalZ=1 AngleXU=0 Radius=4.48111 StartAngle=4.71239 EndAngle=7.85398
    g5: LineSegment StartX=-7.23544 StartY=-4.48111 StartZ=0 EndX=-3.88762 EndY=-4.48111 EndZ=0
    g6: LineSegment StartX=7.23544 StartY=4.48111 StartZ=0 EndX=-7.23544 EndY=4.48111 EndZ=0
    g7: LineSegment StartX=3.88762 StartY=-4.48111 StartZ=0 EndX=7.23544 EndY=-4.48111 EndZ=0
  constraints (11):
    c: Tangent(g1,g0) = -1.5708
    c: Tangent(g0,g2) = -1.5708
    c: PointOnObject(g0,g-2)
    c: Tangent(g3,g5) = -1.5708
    c: Coincident(g7,g4) = -1.5708
    c: Tangent(g4,g6) = -1.5708
    c: Tangent(g6,g3) = -1.5708
    c: Equal(g3,g4)
    c: PointOnObject(g3,g-1)
    c: Coincident(g5,g1)
    c: Coincident(g7,g2)
FEATURE [PartDesign::Pocket] Pocket007
  BaseFeature = -> Fillet010
  Direction = (0,1,-2e-16)
  Length = 21
  Length2 = 5
  Profile = -> Sketch022
  ReferenceAxis = -> Sketch022 [N_Axis]
  Refine = true
  Type = 0
FEATURE [PartDesign::Fillet] Fillet011
  Base = -> Pocket007 [Edge68,Edge58]
  BaseFeature = -> Pocket007
  Radius = 1
  Refine = true
  SupportTransform = false
  UseAllEdges = false
FEATURE [Sketcher::SketchObject] Sketch023
  FullyConstrained = false
  MapMode = 5
  Placement = pos=(0,0,12.5) rot=(0,0,1;0rad)
  Support = -> [Fillet011]
  sketch-geometry (1):
    g0: Circle CenterX=0 CenterY=-20.0878 CenterZ=0 NormalX=0 NormalY=0 NormalZ=1 AngleXU=0 Radius=7.73926
  constraints (1):
    c: PointOnObject(g0,g-2)
FEATURE [PartDesign::Pad] Pad007
  BaseFeature = -> Fillet011
  Direction = (0,0,1)
  Length = 10
  Length2 = 10
  Profile = -> Sketch023
  ReferenceAxis = -> Sketch023 [N_Axis]
  Refine = true
  Type = 0
FEATURE [PartDesign::Fillet] Fillet012
  Base = -> Pad007 [Edge71]
  BaseFeature = -> Pad007
  Radius = 6
  Refine = true
  SupportTransform = false
  UseAllEdges = false
FEATURE [PartDesign::AdditivePipe] AdditivePipe001
  AuxilleryCurvelinear = true
  AuxillerySpineTangent = false
  BaseFeature = -> Fillet012
  Binormal = (0,0,0)
  Mode = 2
  Profile = -> BThreadProfile001
  Refine = true
  Spine = -> Helix001 [Edge1,Edge2,Edge3,Edge4,Edge5,Edge6,Edge7,Edge8,Edge9,Edge10,Edge11,Edge12,Edge13,Edge14,Edge15,Edge16,Edge17,Edge18,Edge19,Edge20,Edge21,Edge22,Edge23,Edge24,Edge25,Edge26,Edge27,Edge28,Edge29,Edge30,Edge31,Edge32,Edge33,Edge34,Edge35,Edge36,Edge37,Edge38,Edge39,Edge40,+8 more]
  SpineTangent = false
  Transformation = 0
  Transition = 0
FEATURE [PartDesign::Body] Body007  label="sjemnik_dlja_rezbi_gayki"
  Group = -> [Sketch021,Pad006,Fillet010,Sketch022,Pocket007,Fillet011,Sketch023,Pad007,BThreadProfile001,Helix001,Fillet012,AdditivePipe001]
  Origin = -> Origin007
  Placement = pos=(0,0,-77) rot=(0,0,1;0rad)
  Tip = -> AdditivePipe001
FEATURE [PartDesign::Plane] DatumPlane002
  AttachmentOffset = pos=(0,0,58) rot=(0,1,0;-1.32645rad)
  Length = 134.47
  MapMode = 45
  Placement = pos=(1.13662e-09,-19.8664,72.5151) rot=(0.001108,0.999999,-0.000866;4.95673rad)
  ResizeMode = 0
  Support = -> [Fillet009]
  Width = 79.5289
FEATURE [Sketcher::SketchObject] Sketch024
  AttachmentOffset = pos=(0,0,-3) rot=(0,0,1;0rad)
  FullyConstrained = false
  MapMode = 5
  Placement = pos=(2.91089,-19.8677,71.7893) rot=(-0.001108,-0.999999,0.000866;1.32645rad)
  Support = -> [DatumPlane002]
  sketch-geometry (1):
    g0: Circle CenterX=-57.5712 CenterY=0 CenterZ=0 NormalX=0 NormalY=0 NormalZ=1 AngleXU=0 Radius=5.01252
  constraints (1):
    c: PointOnObject(g0,g-1)
FEATURE [PartDesign::Pad] Pad008
  BaseFeature = -> Fillet009
  Direction = (-0.970296,0.000418988,0.241922)
  Length = 85
  Length2 = 10
  Profile = -> Sketch024
  ReferenceAxis = -> Sketch024 [N_Axis]
  Refine = true
  Type = 0
FEATURE [PartDesign::Fillet] Fillet013
  Base = -> Pad008 [Face5]
  BaseFeature = -> Pad008
  Radius = 4
  Refine = true
  SupportTransform = false
  UseAllEdges = false
FEATURE [PartDesign::Body] Body006  label="gayka"
  Group = -> [Sketch019,Sketch020,AdditiveLoft,Fillet009,DatumPlane002,Sketch024,Pad008,Fillet013]
  Origin = -> Origin006
  Placement = pos=(0,0,33) rot=(0,0,1;0rad)
  Tip = -> Fillet013
FEATURE [Part::Cut] Cut
  Base = -> Body006
  Refine = true
  Tool = -> Body007
